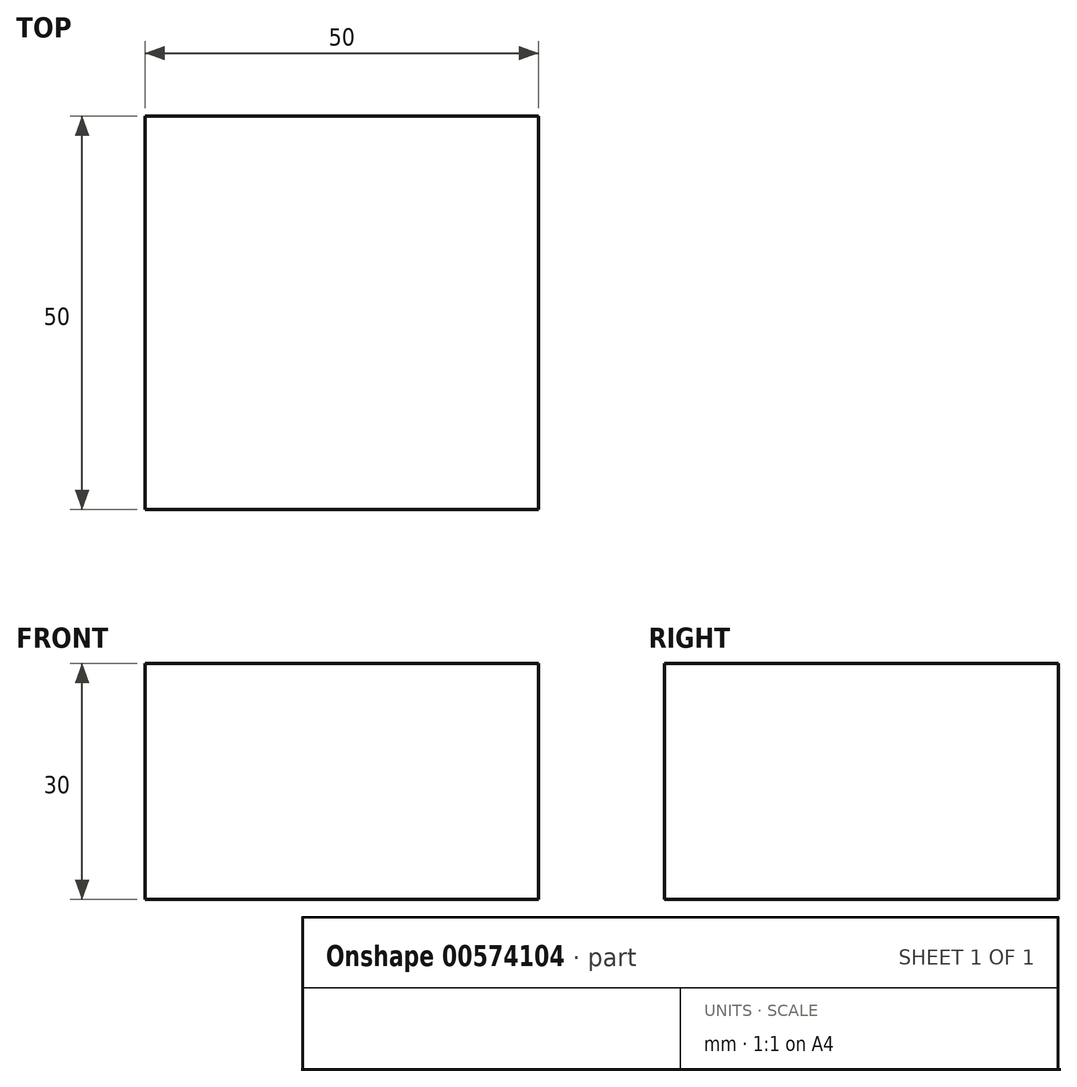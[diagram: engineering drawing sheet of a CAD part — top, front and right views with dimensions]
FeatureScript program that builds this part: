
annotation { "Feature Type Name" : "Feature", "Feature Type Description" : "" }
export const myFeature = defineFeature(function(context is Context, id is Id, definition is map)
    precondition{}
    {
        {
            var Q0;
            Q0=qCreatedBy(makeId("Top.planeOp"),FACE);
            var sketch = newSketch(context, id + "F0", { "sketchPlane" : qUnion([Q0])});
            skLineSegment(sketch, "E0.bottom", {"start": v(-25, 25) * mm, "end": v(25, 25) * mm});
            skLineSegment(sketch, "E0.top", {"start": v(-25, -25) * mm, "end": v(25, -25) * mm});
            skLineSegment(sketch, "E0.left", {"start": v(-25, 25) * mm, "end": v(-25, -25) * mm});
            skLineSegment(sketch, "E0.right", {"start": v(25, 25) * mm, "end": v(25, -25) * mm});
            skSolve(sketch);
        }
        {
            var Q0;
            Q0=makeQuery(id+"F0.imprint","IMPRINT",FACE,{"disambiguationData":[TD([[makeQuery(id+"F0.imprint","IMPRINT",EDGE,{"derivedFrom":sQuery(id+"F0.wireOp",EDGE,"E0.bottom")}),-1.0]])]});
            extrude(context, id + "F1", {"entities" : qUnion([Q0]), "depth" : 30 * mm, "offsetDistance" : 25 * mm});
        }
    });
